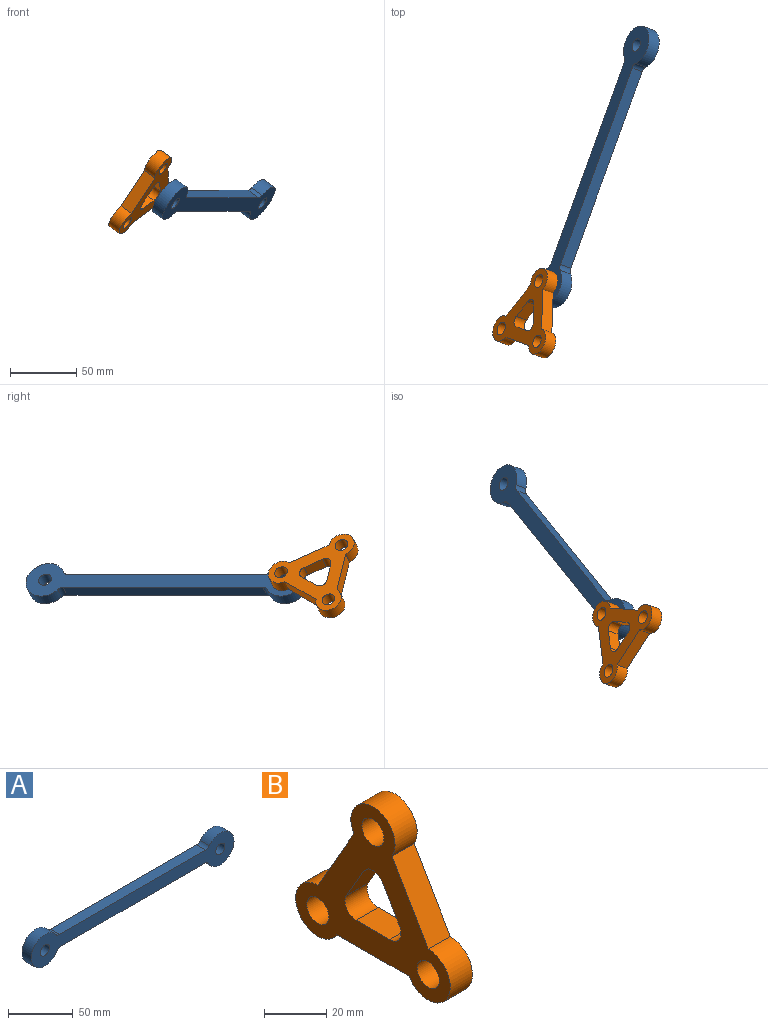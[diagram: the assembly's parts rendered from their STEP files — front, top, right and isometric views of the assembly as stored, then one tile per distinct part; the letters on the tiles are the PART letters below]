
ASSEMBLY  parts=2 mates=1
PART A: 12 faces, bbox 222x10x30 mm
  f0: cylinder r=5mm len=10mm, axis (0,1,0), area 46.4mm2, adj f1,f8,f10,f11
  f1: plane 160x10mm, normal (0,0,1), area 1600mm2, adj f0,f2,f10,f11
  f2: cylinder r=5mm len=10mm, axis (0,1,0), area 46.4mm2, adj f1,f3,f10,f11
  f3: cylinder r=15mm len=30mm, axis (0,1,0), area 767.4mm2, adj f2,f4,f10,f11
  f4: cylinder r=5mm len=10mm, axis (0,1,0), area 52.4mm2, adj f3,f5,f10,f11
  f5: plane 157.36x10mm, normal (0,0,-1), area 1573.6mm2, adj f4,f6,f10,f11
  f6: cylinder r=5mm len=10mm, axis (0,1,0), area 52.4mm2, adj f5,f8,f10,f11
  f7: cylinder r=5mm len=10mm, axis (0,1,0), area 314.2mm2, adj f10,f11
  f8: cylinder r=15mm len=30mm, axis (0,1,0), area 767.4mm2, adj f0,f6,f10,f11
  f9: cylinder r=5mm len=10mm, axis (0,1,0), area 314.2mm2, adj f10,f11
  f10: plane 222x30mm, normal (0,-1,0), area 3216.7mm2, adj f0,f1,f2,f3,f4,f5,f6,f7
  f11: plane 222x30mm, normal (0,1,0), area 3216.7mm2, adj f0,f1,f2,f3,f4,f5,f6,f7
PART B: 17 faces, bbox 10x70x63.3 mm
  f0: plane 32.68x10mm, normal (0,0,-1), area 326.8mm2, adj f1,f14,f15,f16
  f1: cylinder r=10mm len=20mm, axis (-1,0,0), area 418.9mm2, adj f0,f2,f15,f16
  f2: plane 28.3x16.34mm, normal (0,0.87,0.5), area 326.8mm2, adj f1,f3,f15,f16
  f3: cylinder r=10mm len=20mm, axis (-1,0,0), area 418.9mm2, adj f2,f4,f15,f16
  f4: plane 28.3x16.34mm, normal (0,-0.87,0.5), area 326.8mm2, adj f3,f14,f15,f16
  f5: cylinder r=5mm len=10mm, axis (-1,0,0), area 104.7mm2, adj f6,f10,f15,f16
  f6: plane 13.3x10mm, normal (0,0.87,-0.5), area 153.6mm2, adj f5,f7,f15,f16
  f7: cylinder r=5mm len=10mm, axis (-1,0,0), area 104.7mm2, adj f6,f8,f15,f16
  f8: plane 13.3x10mm, normal (0,-0.87,-0.5), area 153.6mm2, adj f7,f9,f15,f16
  f9: cylinder r=5mm len=10mm, axis (-1,0,0), area 104.7mm2, adj f8,f10,f15,f16
  f10: plane 15.36x10mm, normal (0,0,1), area 153.6mm2, adj f5,f9,f15,f16
  f11: cylinder r=5mm len=10mm, axis (-1,0,0), area 314.2mm2, adj f15,f16
  f12: cylinder r=5mm len=10mm, axis (-1,0,0), area 314.2mm2, adj f15,f16
  f13: cylinder r=5mm len=10mm, axis (-1,0,0), area 314.2mm2, adj f15,f16
  f14: cylinder r=10mm len=20mm, axis (-1,0,0), area 418.9mm2, adj f0,f4,f15,f16
  f15: plane 70x63.3mm, normal (1,0,0), area 1684.3mm2, adj f0,f1,f2,f3,f4,f5,f6,f7
  f16: plane 70x63.3mm, normal (-1,0,0), area 1684.3mm2, adj f0,f1,f2,f3,f4,f5,f6,f7
PLACE A rot(axis=(0.56,-0.79,-0.25),160.1deg) t=(-59.65,89.18,-13.5)mm
PLACE B rot(axis=(-0.88,0.46,0.13),91deg) t=(-108.98,-25.75,-6.13)mm
MATE revolute B.f11 <-> A.f8  axis (0.77,-0.28,-0.57) through (-91.4,-1.42,-11.86)mm
